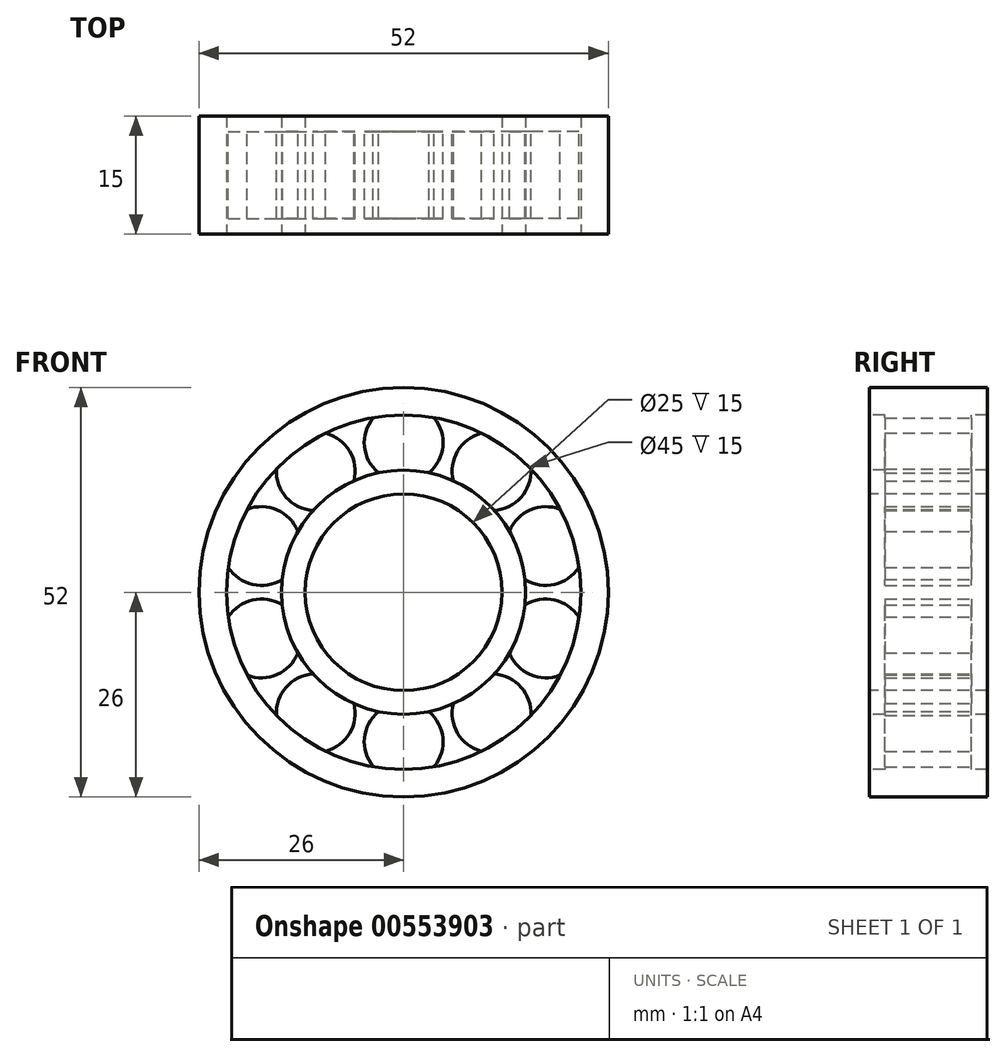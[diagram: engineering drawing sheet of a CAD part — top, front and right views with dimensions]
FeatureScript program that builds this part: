
annotation { "Feature Type Name" : "Feature", "Feature Type Description" : "" }
export const myFeature = defineFeature(function(context is Context, id is Id, definition is map)
    precondition{}
    {
        {
            var Q0;
            Q0=qCreatedBy(makeId("Front.planeOp"),FACE);
            var sketch = newSketch(context, id + "F0", { "sketchPlane" : qUnion([Q0])});
            skCircle(sketch, "E0", {"center": v(0, 0) * mm, "radius": 15.5 * mm});
            skCircle(sketch, "E1", {"center": v(0, 0) * mm, "radius": 12.5 * mm});
            skCircle(sketch, "E2", {"center": v(0, 0) * mm, "radius": 22.5 * mm});
            skCircle(sketch, "E3", {"center": v(0, 0) * mm, "radius": 26 * mm});
            skSolve(sketch);
        }
        {
            var Q0;
            Q0=makeQuery(id+"F0.imprint","IMPRINT",FACE,{"disambiguationData":[TD([[makeQuery(id+"F0.imprint","IMPRINT",EDGE,{"derivedFrom":sQuery(id+"F0.wireOp",EDGE,"E2")}),-1.0]])]});
            var Q1;
            Q1=makeQuery(id+"F0.imprint","IMPRINT",FACE,{"disambiguationData":[TD([[makeQuery(id+"F0.imprint","IMPRINT",EDGE,{"derivedFrom":sQuery(id+"F0.wireOp",EDGE,"E0")}),1.0]])]});
            extrude(context, id + "F1", {"entities" : qUnion([Q0, Q1]), "oppositeDirection" : true, "depth" : 15 * mm, "offsetDistance" : 25 * mm});
        }
        {
            var Q0;
            Q0=qCreatedBy(makeId("Front.planeOp"),FACE);
            cPlane(context, id + "F2", {"entities" : qUnion([Q0]), "cplaneType" : CPlaneType.OFFSET, "offset" : 7.5 * mm, "oppositeDirection" : true, "width" : 150 * mm, "height" : 150 * mm});
        }
        {
            var Q0;
            Q0=qCreatedBy(id+"F2.planeOp",FACE);
            var sketch = newSketch(context, id + "F3", { "sketchPlane" : qUnion([Q0])});
            skCircle(sketch, "E4", {"center": v(0, 19) * mm, "radius": 5 * mm});
            skCircle(sketch, "E5.1.0", {"center": v(-11.17, 15.37) * mm, "radius": 5 * mm});
            skCircle(sketch, "E5.2.0", {"center": v(-18.07, 5.87) * mm, "radius": 5 * mm});
            skCircle(sketch, "E5.3.0", {"center": v(-18.07, -5.87) * mm, "radius": 5 * mm});
            skCircle(sketch, "E5.4.0", {"center": v(-11.17, -15.37) * mm, "radius": 5 * mm});
            skCircle(sketch, "E5.5.0", {"center": v(0, -19) * mm, "radius": 5 * mm});
            skCircle(sketch, "E5.6.0", {"center": v(11.17, -15.37) * mm, "radius": 5 * mm});
            skCircle(sketch, "E5.7.0", {"center": v(18.07, -5.87) * mm, "radius": 5 * mm});
            skCircle(sketch, "E5.8.0", {"center": v(18.07, 5.87) * mm, "radius": 5 * mm});
            skCircle(sketch, "E5.9.0", {"center": v(11.17, 15.37) * mm, "radius": 5 * mm});
            skPoint(sketch, "E5.center", {"position": v(0, 0) * mm});
            skSolve(sketch);
        }
        {
            var Q0;
            Q0=makeQuery(id+"F3.imprint","IMPRINT",FACE,{"disambiguationData":[TD([[makeQuery(id+"F3.imprint","IMPRINT",EDGE,{"derivedFrom":sQuery(id+"F3.wireOp",EDGE,"E4")}),1.0]])]});
            var Q1;
            Q1=makeQuery(id+"F3.imprint","IMPRINT",FACE,{"disambiguationData":[TD([[makeQuery(id+"F3.imprint","IMPRINT",EDGE,{"derivedFrom":sQuery(id+"F3.wireOp",EDGE,"E5.1.0")}),1.0]])]});
            var Q2;
            Q2=makeQuery(id+"F3.imprint","IMPRINT",FACE,{"disambiguationData":[TD([[makeQuery(id+"F3.imprint","IMPRINT",EDGE,{"derivedFrom":sQuery(id+"F3.wireOp",EDGE,"E5.2.0")}),1.0]])]});
            var Q3;
            Q3=makeQuery(id+"F3.imprint","IMPRINT",FACE,{"disambiguationData":[TD([[makeQuery(id+"F3.imprint","IMPRINT",EDGE,{"derivedFrom":sQuery(id+"F3.wireOp",EDGE,"E5.3.0")}),1.0]])]});
            var Q4;
            Q4=makeQuery(id+"F3.imprint","IMPRINT",FACE,{"disambiguationData":[TD([[makeQuery(id+"F3.imprint","IMPRINT",EDGE,{"derivedFrom":sQuery(id+"F3.wireOp",EDGE,"E5.5.0")}),1.0]])]});
            var Q5;
            Q5=makeQuery(id+"F3.imprint","IMPRINT",FACE,{"disambiguationData":[TD([[makeQuery(id+"F3.imprint","IMPRINT",EDGE,{"derivedFrom":sQuery(id+"F3.wireOp",EDGE,"E5.8.0")}),1.0]])]});
            var Q6;
            Q6=makeQuery(id+"F3.imprint","IMPRINT",FACE,{"disambiguationData":[TD([[makeQuery(id+"F3.imprint","IMPRINT",EDGE,{"derivedFrom":sQuery(id+"F3.wireOp",EDGE,"E5.4.0")}),1.0]])]});
            var Q7;
            Q7=makeQuery(id+"F3.imprint","IMPRINT",FACE,{"disambiguationData":[TD([[makeQuery(id+"F3.imprint","IMPRINT",EDGE,{"derivedFrom":sQuery(id+"F3.wireOp",EDGE,"E5.6.0")}),1.0]])]});
            var Q8;
            Q8=makeQuery(id+"F3.imprint","IMPRINT",FACE,{"disambiguationData":[TD([[makeQuery(id+"F3.imprint","IMPRINT",EDGE,{"derivedFrom":sQuery(id+"F3.wireOp",EDGE,"E5.9.0")}),1.0]])]});
            var Q9;
            Q9=makeQuery(id+"F3.imprint","IMPRINT",FACE,{"disambiguationData":[TD([[makeQuery(id+"F3.imprint","IMPRINT",EDGE,{"derivedFrom":sQuery(id+"F3.wireOp",EDGE,"E5.7.0")}),1.0]])]});
            extrude(context, id + "F4", {"entities" : qUnion([Q0, Q1, Q2, Q3, Q4, Q5, Q6, Q7, Q8, Q9]), "operationType" : NewBodyOperationType.ADD, "endBound" : BoundingType.SYMMETRIC, "depth" : 11 * mm, "offsetDistance" : 25 * mm});
        }
    });
